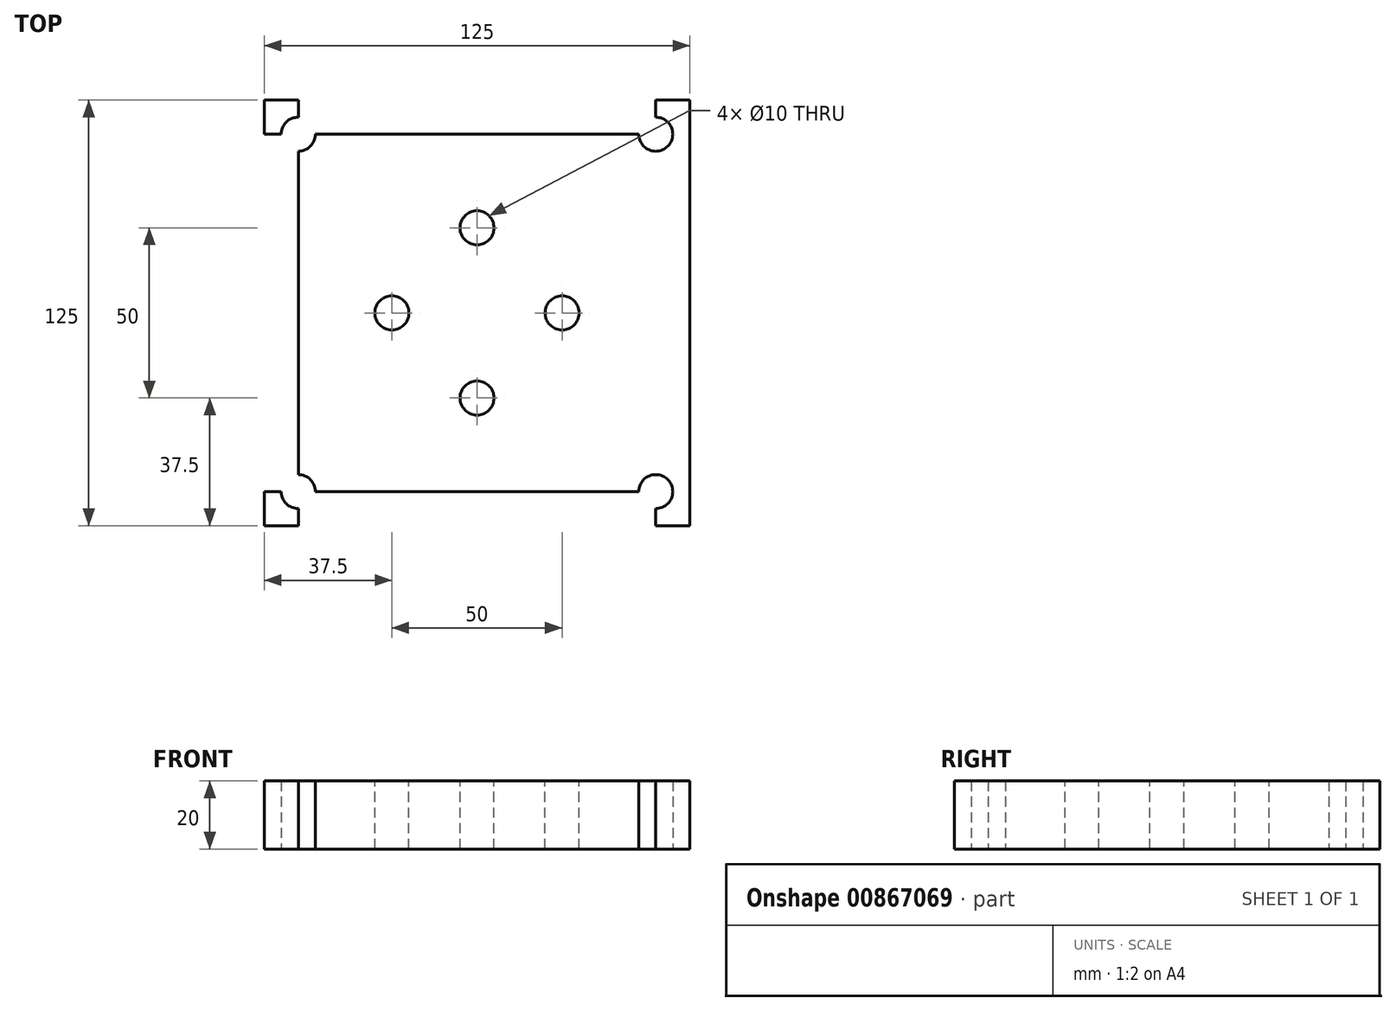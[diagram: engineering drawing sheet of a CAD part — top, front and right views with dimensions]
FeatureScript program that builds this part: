
annotation { "Feature Type Name" : "Feature", "Feature Type Description" : "" }
export const myFeature = defineFeature(function(context is Context, id is Id, definition is map)
    precondition{}
    {
        {
            var Q0;
            Q0=qCreatedBy(makeId("Top.planeOp"),FACE);
            var sketch = newSketch(context, id + "F0", { "sketchPlane" : qUnion([Q0])});
            skLineSegment(sketch, "E0.bottom", {"start": v(62.5, -62.5) * mm, "end": v(-62.5, -62.5) * mm});
            skLineSegment(sketch, "E0.top", {"start": v(62.5, 62.5) * mm, "end": v(-62.5, 62.5) * mm});
            skLineSegment(sketch, "E0.left", {"start": v(62.5, -62.5) * mm, "end": v(62.5, 62.5) * mm});
            skLineSegment(sketch, "E0.right", {"start": v(-62.5, -62.5) * mm, "end": v(-62.5, 62.5) * mm});
            skPoint(sketch, "E0.middle", {"position": v(0, 0) * mm});
            skLineSegment(sketch, "E1", {"start": v(-62.5, -52.5) * mm, "end": v(62.5, -52.5) * mm});
            skLineSegment(sketch, "E2", {"start": v(-52.5, -62.5) * mm, "end": v(-52.5, 62.5) * mm});
            skLineSegment(sketch, "E3", {"start": v(52.5, 62.5) * mm, "end": v(52.5, -62.5) * mm});
            skLineSegment(sketch, "E4", {"start": v(-62.5, 52.5) * mm, "end": v(62.5, 52.5) * mm});
            skLineSegment(sketch, "E5", {"start": v(52.5, -62.5) * mm, "end": v(52.5, -52.5) * mm});
            skLineSegment(sketch, "E6", {"start": v(52.5, -52.5) * mm, "end": v(62.5, -52.5) * mm});
            skLineSegment(sketch, "E7", {"start": v(-62.5, -52.5) * mm, "end": v(-52.5, -52.5) * mm});
            skLineSegment(sketch, "E8", {"start": v(-52.5, -52.5) * mm, "end": v(-52.5, -62.5) * mm});
            skLineSegment(sketch, "E9", {"start": v(-62.5, 52.5) * mm, "end": v(-52.5, 52.5) * mm});
            skLineSegment(sketch, "E10", {"start": v(-52.5, 52.5) * mm, "end": v(-52.5, 62.5) * mm});
            skLineSegment(sketch, "E11", {"start": v(-52.5, -62.5) * mm, "end": v(-52.5, -52.5) * mm});
            skLineSegment(sketch, "E12", {"start": v(52.5, 62.5) * mm, "end": v(52.5, 52.5) * mm});
            skCircle(sketch, "E13", {"center": v(-52.5, 52.5) * mm, "radius": 5 * mm});
            skCircle(sketch, "E14", {"center": v(-52.5, -52.5) * mm, "radius": 5 * mm});
            skCircle(sketch, "E15", {"center": v(52.5, 52.5) * mm, "radius": 5 * mm});
            skCircle(sketch, "E16", {"center": v(52.5, -52.5) * mm, "radius": 5 * mm});
            skCircle(sketch, "E17", {"center": v(0, 0) * mm, "radius": 50 * mm});
            skSolve(sketch);
        }
        {
            var Q0;
            {var subQ1=sQuery(id+"F0.wireOp",EDGE,"E0.right");var subQ5=sQuery(id+"F0.wireOp",EDGE,"E7");var subQ6=makeQuery(id+"F0.imprint","INTERSECT",VERTEX,{"derivedFrom":[subQ1,subQ5]});Q0=makeQuery(id+"F0.imprint","IMPRINT",FACE,{"disambiguationData":[TD([[makeQuery(id+"F0.imprint","IMPRINT",EDGE,{"disambiguationData":[TD([[subQ6,-1.0]])],"derivedFrom":subQ1}),-1.0]])]});}
            var Q1;
            Q1=makeQuery(id+"F0.imprint","IMPRINT",FACE,{"disambiguationData":[TD([[makeQuery(id+"F0.imprint","IMPRINT",EDGE,{"derivedFrom":sQuery(id+"F0.wireOp",EDGE,"E17")}),-1.0]])]});
            var Q2;
            {var subQ1=sQuery(id+"F0.wireOp",EDGE,"E0.top");var subQ7=sQuery(id+"F0.wireOp",EDGE,"E10");var subQ8=makeQuery(id+"F0.imprint","INTERSECT",VERTEX,{"derivedFrom":[subQ1,subQ7]});Q2=makeQuery(id+"F0.imprint","IMPRINT",FACE,{"disambiguationData":[TD([[makeQuery(id+"F0.imprint","IMPRINT",EDGE,{"disambiguationData":[TD([[subQ8,1.0]])],"derivedFrom":subQ1}),1.0]])]});}
            var Q3;
            {var subQ1=sQuery(id+"F0.wireOp",EDGE,"E0.left");var subQ5=sQuery(id+"F0.wireOp",EDGE,"E0.top");var subQ6=makeQuery(id+"F0.imprint","INTERSECT",VERTEX,{"derivedFrom":[subQ5,subQ1]});Q3=makeQuery(id+"F0.imprint","IMPRINT",FACE,{"disambiguationData":[TD([[makeQuery(id+"F0.imprint","IMPRINT",EDGE,{"disambiguationData":[TD([[subQ6,-1.0]])],"derivedFrom":subQ5}),1.0]])]});}
            var Q4;
            {var subQ0=sQuery(id+"F0.wireOp",EDGE,"E4");var subQ1=sQuery(id+"F0.wireOp",EDGE,"E0.left");var subQ2=makeQuery(id+"F0.imprint","INTERSECT",VERTEX,{"derivedFrom":[subQ1,subQ0]});Q4=makeQuery(id+"F0.imprint","IMPRINT",FACE,{"disambiguationData":[TD([[makeQuery(id+"F0.imprint","IMPRINT",EDGE,{"disambiguationData":[TD([[subQ2,1.0]])],"derivedFrom":subQ1}),1.0]])]});}
            var Q5;
            {var subQ1=sQuery(id+"F0.wireOp",EDGE,"E0.left");var subQ6=sQuery(id+"F0.wireOp",EDGE,"E0.bottom");var subQ9=makeQuery(id+"F0.imprint","INTERSECT",VERTEX,{"derivedFrom":[subQ6,subQ1]});Q5=makeQuery(id+"F0.imprint","IMPRINT",FACE,{"disambiguationData":[TD([[makeQuery(id+"F0.imprint","IMPRINT",EDGE,{"disambiguationData":[TD([[subQ9,-1.0]])],"derivedFrom":subQ6}),-1.0]])]});}
            var Q6;
            {var subQ1=sQuery(id+"F0.wireOp",EDGE,"E0.bottom");var subQ5=sQuery(id+"F0.wireOp",EDGE,"E5");var subQ6=makeQuery(id+"F0.imprint","INTERSECT",VERTEX,{"derivedFrom":[subQ1,subQ5]});Q6=makeQuery(id+"F0.imprint","IMPRINT",FACE,{"disambiguationData":[TD([[makeQuery(id+"F0.imprint","IMPRINT",EDGE,{"disambiguationData":[TD([[subQ6,-1.0]])],"derivedFrom":subQ1}),-1.0]])]});}
            var Q7;
            {var subQ1=sQuery(id+"F0.wireOp",EDGE,"E0.right");var subQ5=sQuery(id+"F0.wireOp",EDGE,"E0.bottom");var subQ6=makeQuery(id+"F0.imprint","INTERSECT",VERTEX,{"derivedFrom":[subQ5,subQ1]});Q7=makeQuery(id+"F0.imprint","IMPRINT",FACE,{"disambiguationData":[TD([[makeQuery(id+"F0.imprint","IMPRINT",EDGE,{"disambiguationData":[TD([[subQ6,1.0]])],"derivedFrom":subQ5}),-1.0]])]});}
            var Q8;
            {var subQ1=sQuery(id+"F0.wireOp",EDGE,"E0.right");var subQ5=sQuery(id+"F0.wireOp",EDGE,"E0.top");var subQ6=makeQuery(id+"F0.imprint","INTERSECT",VERTEX,{"derivedFrom":[subQ5,subQ1]});Q8=makeQuery(id+"F0.imprint","IMPRINT",FACE,{"disambiguationData":[TD([[makeQuery(id+"F0.imprint","IMPRINT",EDGE,{"disambiguationData":[TD([[subQ6,1.0]])],"derivedFrom":subQ5}),1.0]])]});}
            var Q9;
            Q9=makeQuery(id+"F0.imprint","IMPRINT",FACE,{"disambiguationData":[TD([[makeQuery(id+"F0.imprint","IMPRINT",EDGE,{"derivedFrom":sQuery(id+"F0.wireOp",EDGE,"E17")}),1.0]])]});
            extrude(context, id + "F1", {"entities" : qUnion([Q0, Q1, Q2, Q3, Q4, Q5, Q6, Q7, Q8, Q9]), "depth" : 20 * mm, "offsetDistance" : 25 * mm});
        }
        {
            var Q0;
            Q0=makeQuery(id+"F1.opExtrude","CAP_FACE",FACE,{"disambiguationData":[OSD([sQuery(id+"F0.wireOp",EDGE,"E0.bottom"),sQuery(id+"F0.wireOp",EDGE,"E0.top"),sQuery(id+"F0.wireOp",EDGE,"E0.left"),sQuery(id+"F0.wireOp",EDGE,"E0.right"),sQuery(id+"F0.wireOp",EDGE,"E13"),sQuery(id+"F0.wireOp",EDGE,"E14"),sQuery(id+"F0.wireOp",EDGE,"E15"),sQuery(id+"F0.wireOp",EDGE,"E16")])],"isStart":false});
            var sketch = newSketch(context, id + "F2", { "sketchPlane" : qUnion([Q0])});
            skCircle(sketch, "E18", {"center": v(0, 0) * mm, "radius": 50 * mm});
            skCircle(sketch, "E19", {"center": v(0, 0) * mm, "radius": 40 * mm});
            skCircle(sketch, "E20", {"center": v(-25, 0) * mm, "radius": 5 * mm});
            skCircle(sketch, "E21", {"center": v(25, 0) * mm, "radius": 5 * mm});
            skCircle(sketch, "E22", {"center": v(0, 25) * mm, "radius": 5 * mm});
            skCircle(sketch, "E23", {"center": v(0, -25) * mm, "radius": 5 * mm});
            skSolve(sketch);
        }
        {
            var Q0;
            Q0=makeQuery(id+"F2.imprint","IMPRINT",FACE,{"disambiguationData":[TD([[makeQuery(id+"F2.imprint","IMPRINT",EDGE,{"derivedFrom":sQuery(id+"F2.wireOp",EDGE,"E20")}),1.0]])]});
            var Q1;
            Q1=makeQuery(id+"F2.imprint","IMPRINT",FACE,{"disambiguationData":[TD([[makeQuery(id+"F2.imprint","IMPRINT",EDGE,{"derivedFrom":sQuery(id+"F2.wireOp",EDGE,"E22")}),1.0]])]});
            var Q2;
            Q2=makeQuery(id+"F2.imprint","IMPRINT",FACE,{"disambiguationData":[TD([[makeQuery(id+"F2.imprint","IMPRINT",EDGE,{"derivedFrom":sQuery(id+"F2.wireOp",EDGE,"E21")}),1.0]])]});
            var Q3;
            Q3=makeQuery(id+"F2.imprint","IMPRINT",FACE,{"disambiguationData":[TD([[makeQuery(id+"F2.imprint","IMPRINT",EDGE,{"derivedFrom":sQuery(id+"F2.wireOp",EDGE,"E23")}),1.0]])]});
            extrude(context, id + "F3", {"entities" : qUnion([Q0, Q1, Q2, Q3]), "operationType" : NewBodyOperationType.REMOVE, "oppositeDirection" : true, "depth" : 25 * mm, "offsetDistance" : 25 * mm});
        }
    });
